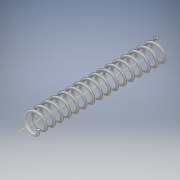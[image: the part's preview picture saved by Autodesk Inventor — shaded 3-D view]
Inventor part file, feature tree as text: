
AUTODESK INVENTOR PART (.ipt)
format: ipt  version: 2018 (Build 220112000, 112)  size: 314,368 bytes
history: native  units: mm
features: sketch x2, helix x1, other x1
ambient origin geometry x8: Origin, YZ Plane, XZ Plane, XY Plane, X Axis, Y Axis, Z Axis, Center Point
bodies: Solid1 (feature_tree)
feature tree (4):
  helix  "Coil1"  [1 undecoded]
  sketch  "Sketch2"  dims[d2=1.6mm d3=1.5mm d4=25.0mm d5=10.0mm d6=0.0mm d7=90.0deg d8=90.0deg d9=0.0mm d10=0.0mm]
  other  "Work Axis1"
  sketch  "Sketch1"  dims[d1=0.5mm]
note: 1 required parameter value undecoded (feature->parameter linkage not recoverable at this tier; creation-order binding heuristic only, values carry confidence <= 0.55)
